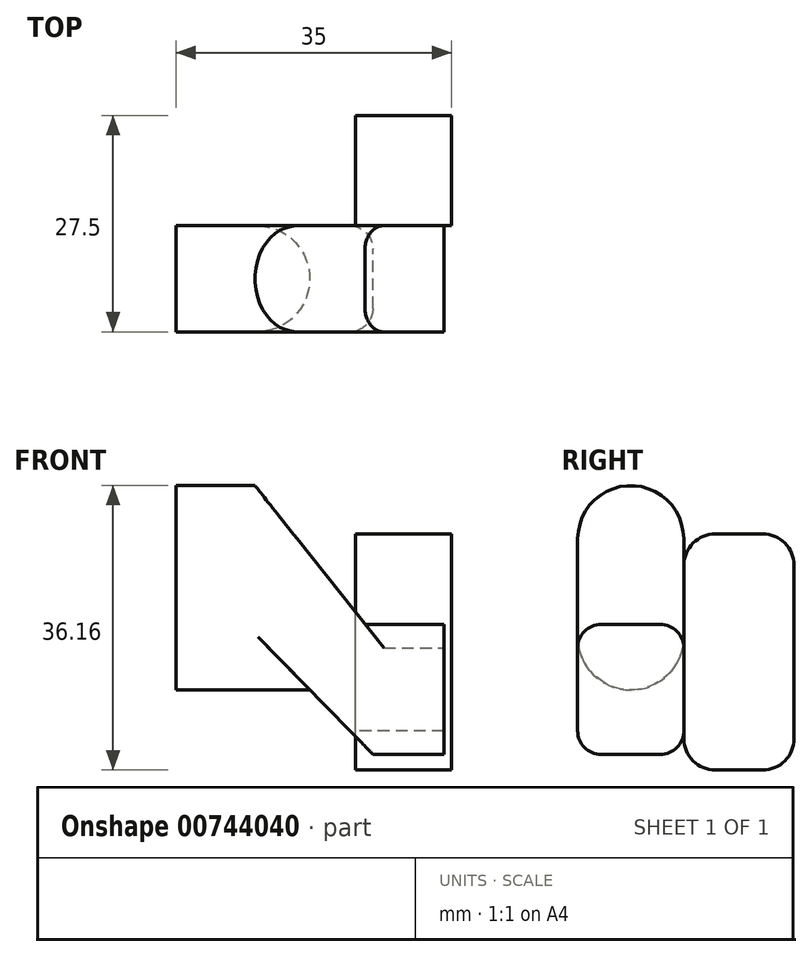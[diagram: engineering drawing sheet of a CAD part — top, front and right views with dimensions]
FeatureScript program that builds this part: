
annotation { "Feature Type Name" : "Feature", "Feature Type Description" : "" }
export const myFeature = defineFeature(function(context is Context, id is Id, definition is map)
    precondition{}
    {
        {
            var Q0;
            Q0=qCreatedBy(makeId("Front.planeOp"),FACE);
            var sketch = newSketch(context, id + "F0", { "sketchPlane" : qUnion([Q0])});
            skLineSegment(sketch, "E0", {"start": v(0, 0) * mm, "end": v(0, 26) * mm});
            skLineSegment(sketch, "E1", {"start": v(0, 26) * mm, "end": v(10, 26) * mm});
            skLineSegment(sketch, "E2", {"start": v(10, 26) * mm, "end": v(24, 8.34) * mm});
            skLineSegment(sketch, "E3", {"start": v(24, 8.34) * mm, "end": v(34, 8.34) * mm});
            skLineSegment(sketch, "E4", {"start": v(34, 8.34) * mm, "end": v(34, -8.16) * mm});
            skLineSegment(sketch, "E5", {"start": v(34, -8.16) * mm, "end": v(25, -8.16) * mm});
            skLineSegment(sketch, "E6", {"start": v(25, -8.16) * mm, "end": v(17, 0) * mm});
            skLineSegment(sketch, "E7", {"start": v(17, 0) * mm, "end": v(0, 0) * mm});
            skSolve(sketch);
        }
        {
            var Q0;
            Q0 = qSketchRegion(id + "F0", true);
            extrude(context, id + "F1", {"entities" : qUnion([Q0]), "depth" : 13.5 * mm, "offsetDistance" : 25 * mm});
        }
        {
            var Q0;
            Q0=makeQuery(id+"F1.opExtrude","CAP_EDGE",EDGE,{"disambiguationData":[OSD([sQuery(id+"F0.wireOp",EDGE,"E1")])],"isStart":true});
            var Q1;
            Q1=makeQuery(id+"F1.opExtrude","CAP_EDGE",EDGE,{"disambiguationData":[OSD([sQuery(id+"F0.wireOp",EDGE,"E1")])],"isStart":false});
            var Q2;
            Q2=makeQuery(id+"F1.opExtrude","CAP_EDGE",EDGE,{"disambiguationData":[OSD([sQuery(id+"F0.wireOp",EDGE,"E7")])],"isStart":true});
            var Q3;
            Q3=makeQuery(id+"F1.opExtrude","CAP_EDGE",EDGE,{"disambiguationData":[OSD([sQuery(id+"F0.wireOp",EDGE,"E7")])],"isStart":false});
            fillet(context, id + "F2", {"entities" : qUnion([Q0, Q1, Q2, Q3]), "radius" : 6.75 * mm, "tangentPropagation" : true, "allowEdgeOverflow" : false});
        }
        {
            var Q0;
            Q0=makeQuery(id+"F1.opExtrude","CAP_EDGE",EDGE,{"disambiguationData":[OSD([sQuery(id+"F0.wireOp",EDGE,"E3")])],"isStart":false});
            var Q1;
            Q1=makeQuery(id+"F1.opExtrude","CAP_EDGE",EDGE,{"disambiguationData":[OSD([sQuery(id+"F0.wireOp",EDGE,"E3")])],"isStart":true});
            var Q2;
            Q2=makeQuery(id+"F1.opExtrude","CAP_EDGE",EDGE,{"disambiguationData":[OSD([sQuery(id+"F0.wireOp",EDGE,"E5")])],"isStart":true});
            var Q3;
            Q3=makeQuery(id+"F1.opExtrude","CAP_EDGE",EDGE,{"disambiguationData":[OSD([sQuery(id+"F0.wireOp",EDGE,"E5")])],"isStart":false});
            fillet(context, id + "F3", {"entities" : qUnion([Q0, Q1, Q2, Q3]), "radius" : 3 * mm, "tangentPropagation" : true, "allowEdgeOverflow" : false});
        }
        {
            var Q0;
            Q0=makeQuery(id+"F1.opExtrude","CAP_FACE",FACE,{"disambiguationData":[OSD([sQuery(id+"F0.wireOp",EDGE,"E0"),sQuery(id+"F0.wireOp",EDGE,"E1"),sQuery(id+"F0.wireOp",EDGE,"E2"),sQuery(id+"F0.wireOp",EDGE,"E3"),sQuery(id+"F0.wireOp",EDGE,"E4"),sQuery(id+"F0.wireOp",EDGE,"E5"),sQuery(id+"F0.wireOp",EDGE,"E6"),sQuery(id+"F0.wireOp",EDGE,"E7")])],"isStart":true});
            var sketch = newSketch(context, id + "F4", { "sketchPlane" : qUnion([Q0])});
            skLineSegment(sketch, "E8.bottom", {"start": v(-35, -10.16) * mm, "end": v(-22.76, -10.16) * mm});
            skLineSegment(sketch, "E8.top", {"start": v(-35, 19.84) * mm, "end": v(-22.76, 19.84) * mm});
            skLineSegment(sketch, "E8.left", {"start": v(-35, -10.16) * mm, "end": v(-35, 19.84) * mm});
            skLineSegment(sketch, "E8.right", {"start": v(-22.76, -10.16) * mm, "end": v(-22.76, 19.84) * mm});
            skSolve(sketch);
        }
        {
            var Q0;
            Q0 = qSketchRegion(id + "F4", true);
            extrude(context, id + "F5", {"entities" : qUnion([Q0]), "operationType" : NewBodyOperationType.ADD, "depth" : 14 * mm, "offsetDistance" : 25 * mm});
        }
        {
            var Q0;
            Q0=makeQuery(id+"F5.opExtrude","CAP_EDGE",EDGE,{"disambiguationData":[OSD([sQuery(id+"F4.wireOp",EDGE,"E8.top")])],"isStart":false});
            var Q1;
            Q1=makeQuery(id+"F5.opExtrude","CAP_EDGE",EDGE,{"disambiguationData":[OSD([sQuery(id+"F4.wireOp",EDGE,"E8.top")])],"isStart":true});
            var Q2;
            Q2=makeQuery(id+"F5.opExtrude","CAP_EDGE",EDGE,{"disambiguationData":[OSD([sQuery(id+"F4.wireOp",EDGE,"E8.bottom")])],"isStart":false});
            var Q3;
            Q3=makeQuery(id+"F5.opExtrude","CAP_EDGE",EDGE,{"disambiguationData":[OSD([sQuery(id+"F4.wireOp",EDGE,"E8.bottom")])],"isStart":true});
            fillet(context, id + "F6", {"entities" : qUnion([Q0, Q1, Q2, Q3]), "radius" : 4 * mm, "tangentPropagation" : true, "allowEdgeOverflow" : false});
        }
    });
